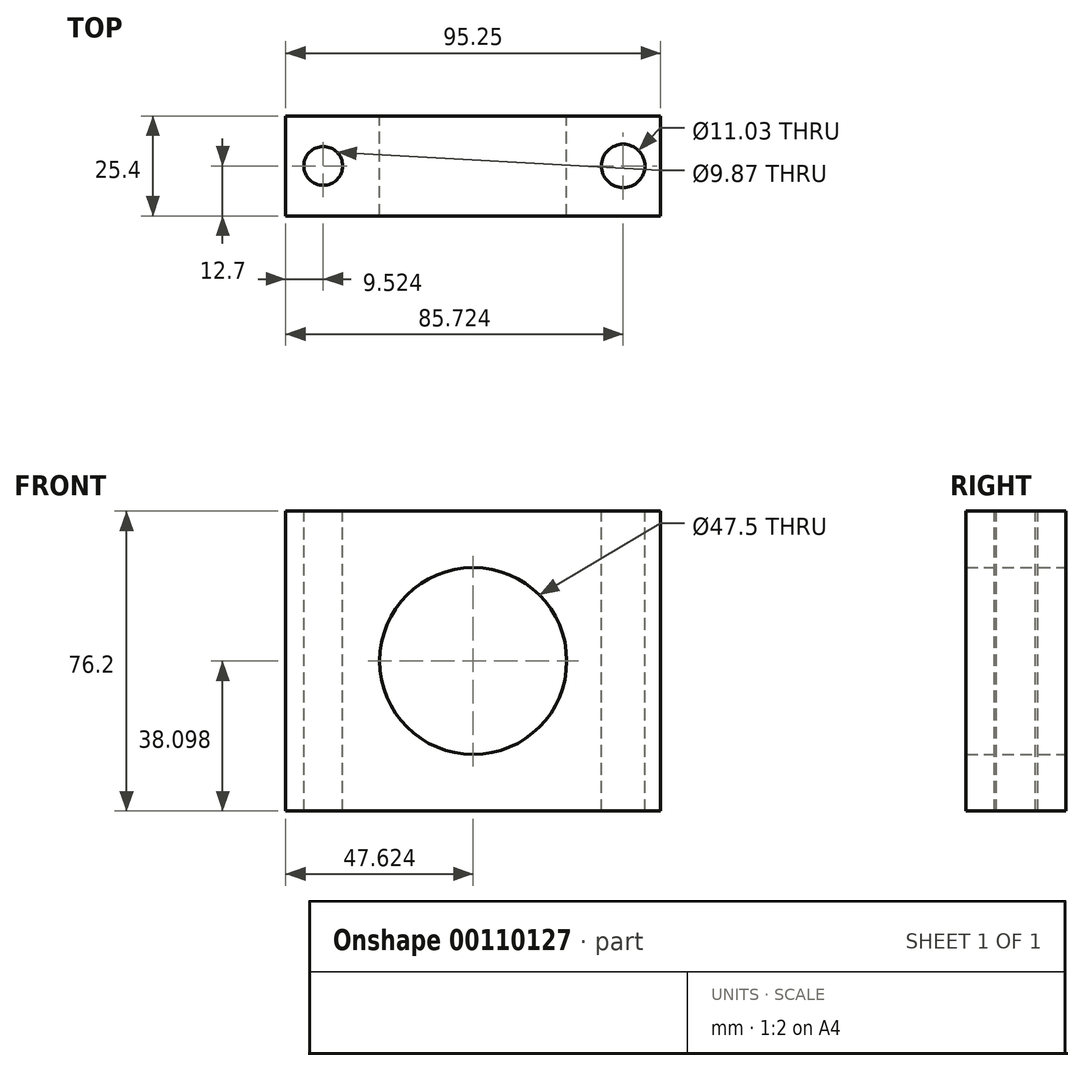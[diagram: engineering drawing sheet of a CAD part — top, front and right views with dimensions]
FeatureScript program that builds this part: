
annotation { "Feature Type Name" : "Feature", "Feature Type Description" : "" }
export const myFeature = defineFeature(function(context is Context, id is Id, definition is map)
    precondition{}
    {
        {
            var Q0;
            Q0=qCreatedBy(makeId("Front.planeOp"),FACE);
            var sketch = newSketch(context, id + "F0", { "sketchPlane" : qUnion([Q0])});
            skLineSegment(sketch, "E0", {"start": v(-46.07, 61.8) * mm, "end": v(-46.07, -14.4) * mm});
            skLineSegment(sketch, "E1", {"start": v(-46.07, -14.4) * mm, "end": v(49.18, -14.4) * mm});
            skLineSegment(sketch, "E2", {"start": v(49.18, -14.4) * mm, "end": v(49.18, 61.8) * mm});
            skLineSegment(sketch, "E3", {"start": v(49.18, 61.8) * mm, "end": v(-46.07, 61.8) * mm});
            skCircle(sketch, "E4", {"center": v(1.55, 23.7) * mm, "radius": 23.75 * mm});
            skPoint(sketch, "E4.centerSnap0", {"position": v(-46.07, 23.7) * mm});
            skPoint(sketch, "E4.centerSnap1", {"position": v(1.55, 61.8) * mm});
            skSolve(sketch);
        }
        {
            var Q0;
            Q0=makeQuery(id+"F0.imprint","IMPRINT",FACE,{"disambiguationData":[TD([[makeQuery(id+"F0.imprint","IMPRINT",EDGE,{"derivedFrom":sQuery(id+"F0.wireOp",EDGE,"E0")}),1.0]])]});
            extrude(context, id + "F1", {"entities" : qUnion([Q0]), "depth" : 25.4 * mm});
        }
        {
            var Q0;
            Q0=makeQuery(id+"F1.opExtrude","SWEPT_FACE",FACE,{"disambiguationData":[OSD([sQuery(id+"F0.wireOp",EDGE,"E3")])]});
            var sketch = newSketch(context, id + "F2", { "sketchPlane" : qUnion([Q0])});
            skCircle(sketch, "E5", {"center": v(-36.55, -12.7) * mm, "radius": 4.93 * mm});
            skCircle(sketch, "E6", {"center": v(39.65, -12.7) * mm, "radius": 5.52 * mm});
            skSolve(sketch);
        }
        {
            var Q0;
            Q0 = qSketchRegion(id + "F2", true);
            extrude(context, id + "F3", {"entities" : qUnion([Q0]), "operationType" : NewBodyOperationType.REMOVE, "oppositeDirection" : true, "depth" : 113.8 * mm});
        }
    });
